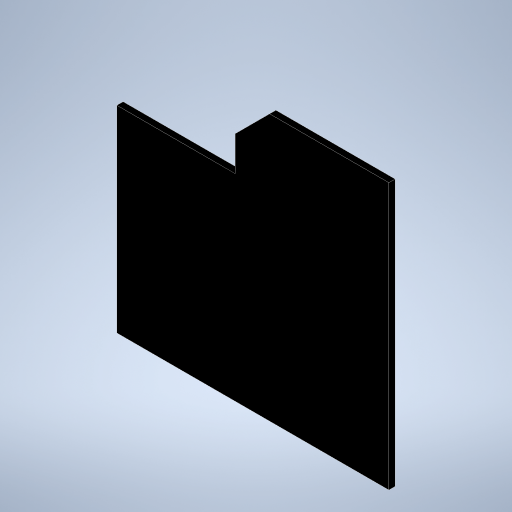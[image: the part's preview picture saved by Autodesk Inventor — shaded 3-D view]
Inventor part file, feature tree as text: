
AUTODESK INVENTOR PART (.ipt)
format: ipt  version: 2023.2 (Build 272271000, 271)  size: 208,384 bytes
history: native  units: in
note: dims shown in document units (in); Inventor stores cm internally (conversion verified against a paired STEP export)
features: other x1, extrude x1, sketch x1
ambient origin geometry x8: Origin, YZ Plane, XZ Plane, XY Plane, X Axis, Y Axis, Z Axis, Center Point
bodies: Solid1 (feature_tree)
feature tree (3):
  other  "BoardFrontPlane"
  extrude  "BoardOutline"  [1 undecoded]
  sketch  "Sketch1"  dims[d0=0.0638in d1=0.0in]
note: 1 required parameter value undecoded (feature->parameter linkage not recoverable at this tier; creation-order binding heuristic only, values carry confidence <= 0.55)
